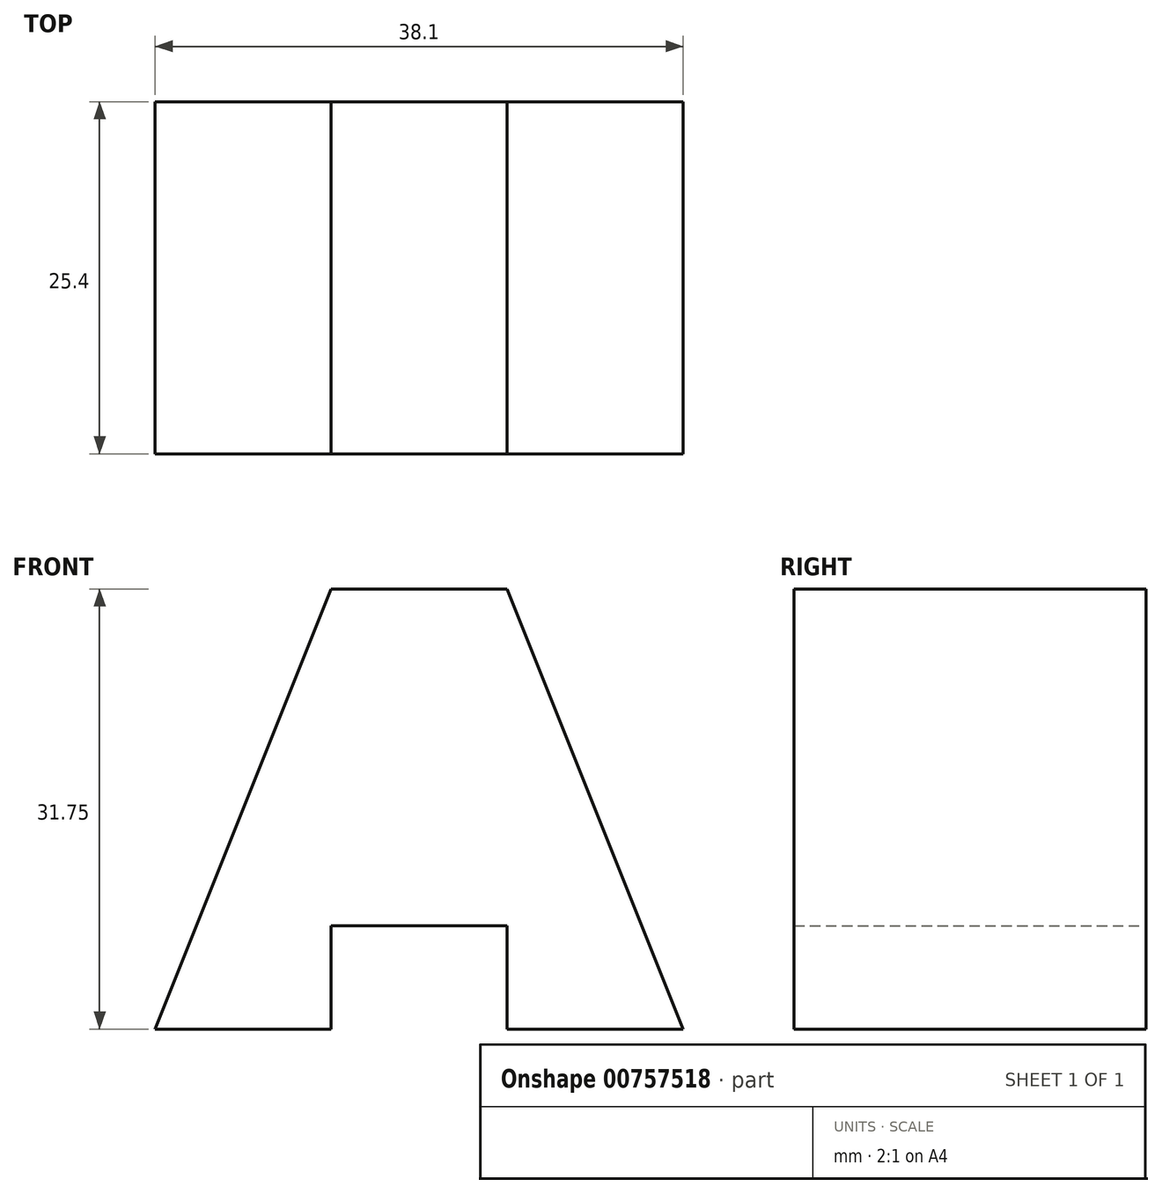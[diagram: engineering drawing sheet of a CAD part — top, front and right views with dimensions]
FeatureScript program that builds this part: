
annotation { "Feature Type Name" : "Feature", "Feature Type Description" : "" }
export const myFeature = defineFeature(function(context is Context, id is Id, definition is map)
    precondition{}
    {
        {
            var Q0;
            Q0=qCreatedBy(makeId("Front.planeOp"),FACE);
            var sketch = newSketch(context, id + "F0", { "sketchPlane" : qUnion([Q0])});
            skLineSegment(sketch, "E0", {"start": v(0, 0) * mm, "end": v(0, 31.75) * mm});
            skLineSegment(sketch, "E1", {"start": v(0, 31.75) * mm, "end": v(-38.1, 31.75) * mm});
            skLineSegment(sketch, "E2", {"start": v(-38.1, 31.75) * mm, "end": v(-38.1, 0) * mm});
            skLineSegment(sketch, "E3", {"start": v(-38.1, 0) * mm, "end": v(0, 0) * mm});
            skSolve(sketch);
        }
        {
            var Q0;
            Q0 = qSketchRegion(id + "F0", true);
            extrude(context, id + "F1", {"entities" : qUnion([Q0]), "depth" : 25.4 * mm, "offsetDistance" : 25.4 * mm});
        }
        {
            var Q0;
            Q0=makeQuery(id+"F1.opExtrude","CAP_FACE",FACE,{"disambiguationData":[OSD([sQuery(id+"F0.wireOp",EDGE,"E0"),sQuery(id+"F0.wireOp",EDGE,"E1"),sQuery(id+"F0.wireOp",EDGE,"E2"),sQuery(id+"F0.wireOp",EDGE,"E3")])],"isStart":true});
            var sketch = newSketch(context, id + "F2", { "sketchPlane" : qUnion([Q0])});
            skLineSegment(sketch, "E4", {"start": v(25.4, 31.75) * mm, "end": v(38.1, 0) * mm});
            skLineSegment(sketch, "E5", {"start": v(38.1, 0) * mm, "end": v(25.4, 0) * mm});
            skLineSegment(sketch, "E6", {"start": v(25.4, 0) * mm, "end": v(25.4, 7.45) * mm});
            skLineSegment(sketch, "E7", {"start": v(25.4, 7.45) * mm, "end": v(12.7, 7.45) * mm});
            skLineSegment(sketch, "E8", {"start": v(12.7, 7.45) * mm, "end": v(12.7, 0) * mm});
            skLineSegment(sketch, "E9", {"start": v(12.7, 0) * mm, "end": v(0, 0) * mm});
            skLineSegment(sketch, "E10", {"start": v(0, 0) * mm, "end": v(12.7, 31.75) * mm});
            skLineSegment(sketch, "E11", {"start": v(12.7, 31.75) * mm, "end": v(25.4, 31.75) * mm});
            skSolve(sketch);
        }
        {
            var Q0;
            {var subQ0=sQuery(id+"F2.wireOp",EDGE,"E10");Q0=makeQuery(id+"F2.imprint","IMPRINT",FACE,{"disambiguationData":[TD([[makeQuery(id+"F2.imprint","IMPRINT",EDGE,{"derivedFrom":subQ0}),1.0]])]});}
            var Q1;
            {var subQ0=sQuery(id+"F2.wireOp",EDGE,"E4");Q1=makeQuery(id+"F2.imprint","IMPRINT",FACE,{"disambiguationData":[TD([[makeQuery(id+"F2.imprint","IMPRINT",EDGE,{"derivedFrom":subQ0}),1.0]])]});}
            var Q2;
            {var subQ0=sQuery(id+"F2.wireOp",EDGE,"E6");Q2=makeQuery(id+"F2.imprint","IMPRINT",FACE,{"disambiguationData":[TD([[makeQuery(id+"F2.imprint","IMPRINT",EDGE,{"derivedFrom":subQ0}),1.0]])]});}
            extrude(context, id + "F3", {"entities" : qUnion([Q0, Q1, Q2]), "operationType" : NewBodyOperationType.REMOVE, "endBound" : BoundingType.THROUGH_ALL, "oppositeDirection" : true, "depth" : 25.4 * mm, "offsetDistance" : 25.4 * mm});
        }
    });
